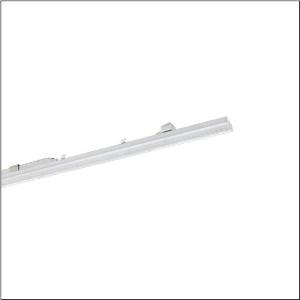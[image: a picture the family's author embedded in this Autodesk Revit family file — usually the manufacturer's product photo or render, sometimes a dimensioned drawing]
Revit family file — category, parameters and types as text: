
# Revit family: tl_l_5wd7a8f0h2b5
name_source: partatom
category: Lighting Fixtures
units: mm (PartAtom-declared; Revit-internal decimal feet)

## family parameters
Cut with Voids When Loaded = No
Host = Face
Light Source = No
Part Type = Normal
Room Calculation Point = No
Round Connector Dimension = Use Diameter
Shared = No

## types (1)
- TL L (1 x LED, 4990 lm, 30 W, 4000K)
    Apparent Load = 30 VA
    CIE Flux Codes = 49 84 98 100 100
    Color Rendering = 80
    Color Temperature = 4000K
    Default Elevation = 1800 mm
    Description = TL L, luminaire insert, of sheet steel, galvanised, coil coated, white, length: 1.500mm, width: 66mm, height: 67mm, surge protection,LED rated luminous flux: 4.990lm, light colour: 840, control gear: 4..20mA, with terminal, 5-pole, mains connection: 230..240V, AC, 50/60Hz, rated input power: 30W, micro fuse,primary optical cover: cover, of PMMA, light emission: direct distribution, protection rating (complete): as luminaire, insulation class (complete): insulation class I (protective earthing), certification: CE, impact resistance: IK06, permissible ambient temperature for indoor applications: -25..+35°C, packaging unit: 1 piece
    Height = 120 mm
    Lamp = 1 x LED
    Lamp Light Flux = 4990 lm
    Lamp Power = 30 W
    Lamp count = 1
    Length = 1690 mm
    Luminous efficacy = 166 lm/W
    Manufacturer = Siteco
    ModVariant = No
    Model = 5WD7A8F0H2B5
    Mounting Place = Ceiling
    Mounting Type = Pendant
    Number of Poles = 1
    OnlyDefault = Yes
    Power Factor = 1
    Product Name = TL L
    Product group = luminaire insert
    ProductGroupID = 901
    Protection Class = Protection class I
    Protection Degree = Degree of protection
    RLX_Detail_Level = 1
    RLX_Emergency_Light_Flux = 0 lm
    RLX_Emergency_Type = 0
    RLX_Emergency_Type_DB = No
    RlxData = <blob elided: 14133 chars, md5=5bbeaa0b>
    Socket = socket
    Standby Power = 0 W
    System Light Flux = 4990 lm
    System Power = 30 W
    Type Comments = Product without accessories
    Type Image = l_1294382.jpg
    URL = http://relux.com
    VarID = ---
    Voltage = 0 V
    Weight = 0.00 kg
    Width = 208 mm

## geometry (parser evidence)
native form markers: Sweep x11
no freeform markers — native parametric forms only
